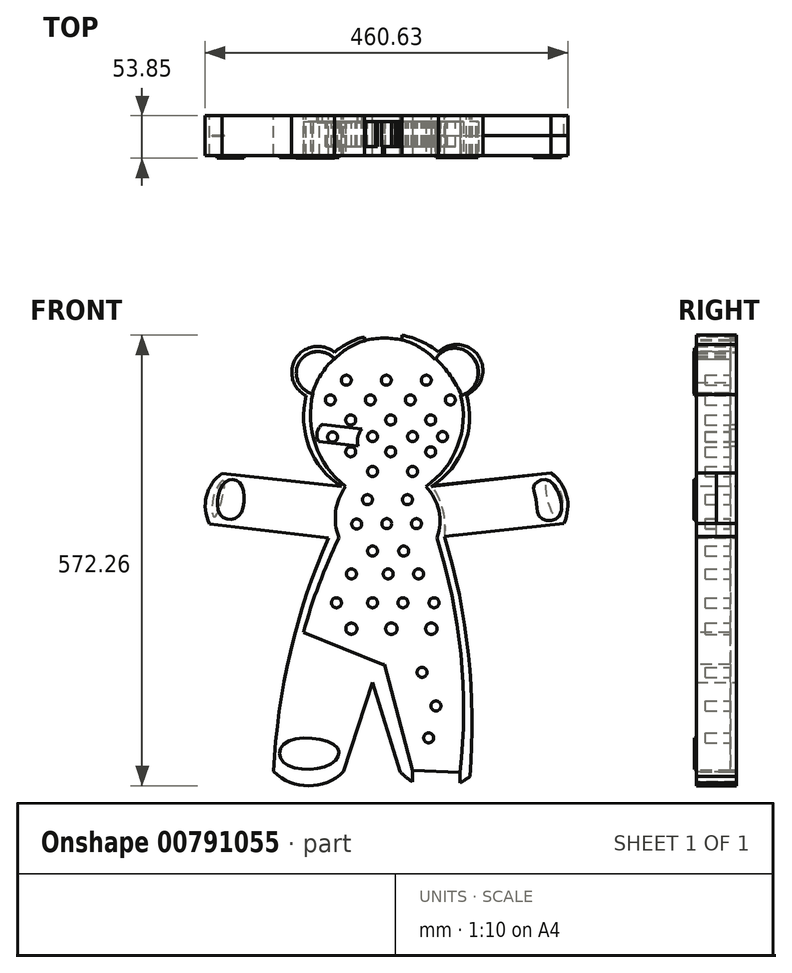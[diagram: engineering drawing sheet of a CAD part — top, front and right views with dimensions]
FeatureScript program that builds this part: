
annotation { "Feature Type Name" : "Feature", "Feature Type Description" : "" }
export const myFeature = defineFeature(function(context is Context, id is Id, definition is map)
    precondition{}
    {
        {
            var Q0;
            Q0=qCreatedBy(makeId("Front.planeOp"),FACE);
            var sketch = newSketch(context, id + "F0", { "sketchPlane" : qUnion([Q0])});
            skArc(sketch, "E0", {"start": v(-48.62, 60.53) * mm, "mid": v(-97.36, 52.98) * mm, "end": v(-84.24, 5.44) * mm});
            skArc(sketch, "E1", {"start": v(119.34, 6.7) * mm, "mid": v(134.68, 55.52) * mm, "end": v(83.78, 60.76) * mm});
            skArc(sketch, "E2", {"start": v(-84.24, 5.44) * mm, "mid": v(-80.59, -59.54) * mm, "end": v(-39.49, -110) * mm});
            skArc(sketch, "E3.trimOffspring", {"start": v(83.78, 60.76) * mm, "mid": v(17.54, 84.02) * mm, "end": v(-48.62, 60.53) * mm});
            skPoint(sketch, "E4.orphan", {"position": v(-45.78, 57.89) * mm});
            skPoint(sketch, "E5.orphan", {"position": v(81.22, 57.89) * mm});
            skLineSegment(sketch, "E6", {"start": v(-39.49, -110) * mm, "end": v(-190.95, -93.16) * mm});
            skLineSegment(sketch, "E7", {"start": v(74.93, -110) * mm, "end": v(226.37, -92.87) * mm});
            skArc(sketch, "E8", {"start": v(-190.95, -93.16) * mm, "mid": v(-211.02, -122.3) * mm, "end": v(-207.2, -157.48) * mm});
            skArc(sketch, "E9", {"start": v(242.9, -156.82) * mm, "mid": v(246.44, -121.8) * mm, "end": v(226.37, -92.87) * mm});
            skLineSegment(sketch, "E10", {"start": v(-207.2, -157.48) * mm, "end": v(-55.83, -175.25) * mm});
            skLineSegment(sketch, "E11", {"start": v(242.9, -156.82) * mm, "end": v(91.38, -173.24) * mm});
            skPoint(sketch, "E12.end.orphan", {"position": v(-138.9, -276.85) * mm});
            skArc(sketch, "E13.trimOffspring", {"start": v(74.93, -110) * mm, "mid": v(116.27, -58.92) * mm, "end": v(119.34, 6.7) * mm});
            skArc(sketch, "E14", {"start": v(-55.83, -175.25) * mm, "mid": v(-104.52, -320.36) * mm, "end": v(-125.58, -471.96) * mm});
            skArc(sketch, "E15", {"start": v(123.63, -478.04) * mm, "mid": v(121.78, -324.13) * mm, "end": v(91.38, -173.24) * mm});
            skArc(sketch, "E16", {"start": v(-125.58, -471.96) * mm, "mid": v(-81.13, -490.11) * mm, "end": v(-36.68, -471.96) * mm});
            skArc(sketch, "E17", {"start": v(34.73, -471.96) * mm, "mid": v(77.94, -493.21) * mm, "end": v(123.63, -478.04) * mm});
            skLineSegment(sketch, "E18", {"start": v(-36.68, -471.96) * mm, "end": v(0, -358.61) * mm});
            skLineSegment(sketch, "E19", {"start": v(0, -358.61) * mm, "end": v(34.73, -471.96) * mm});
            skSolve(sketch);
        }
        {
            var Q0;
            Q0=makeQuery(id+"F0.imprint","IMPRINT",FACE,{"disambiguationData":[TD([[makeQuery(id+"F0.imprint","IMPRINT",EDGE,{"derivedFrom":sQuery(id+"F0.wireOp",EDGE,"E0")}),1.0]])]});
            var sketch = newSketch(context, id + "F1", { "sketchPlane" : qUnion([Q0])});
            skArc(sketch, "E20", {"start": v(-40.72, -110.17) * mm, "mid": v(-55.88, -141.35) * mm, "end": v(-55.5, -176.02) * mm});
            skArc(sketch, "E21", {"start": v(91.74, -173.3) * mm, "mid": v(89.43, -139.67) * mm, "end": v(75.28, -109.08) * mm});
            skLineSegment(sketch, "E22", {"start": v(-190.93, -92.66) * mm, "end": v(-40.72, -110.17) * mm});
            skArc(sketch, "E23", {"start": v(-190.93, -92.66) * mm, "mid": v(-211, -122.25) * mm, "end": v(-206.68, -157.73) * mm});
            skLineSegment(sketch, "E24", {"start": v(-206.68, -157.73) * mm, "end": v(-55.5, -176.02) * mm});
            skLineSegment(sketch, "E25", {"start": v(75.28, -109.08) * mm, "end": v(226.9, -92.64) * mm});
            skArc(sketch, "E26", {"start": v(243.25, -155.89) * mm, "mid": v(246.19, -121.4) * mm, "end": v(226.9, -92.64) * mm});
            skLineSegment(sketch, "E27", {"start": v(91.74, -173.3) * mm, "end": v(243.25, -155.89) * mm});
            skSolve(sketch);
        }
        {
            var Q0;
            Q0 = qSketchRegion(id + "F1", true);
            extrude(context, id + "F2", {"entities" : qUnion([Q0]), "depth" : 25.4 * mm, "offsetDistance" : 25.4 * mm});
        }
        {
            var Q0;
            Q0=makeQuery(id+"F2.opExtrude","CAP_FACE",FACE,{"disambiguationData":[OSD([sQuery(id+"F1.wireOp",EDGE,"E20"),sQuery(id+"F1.wireOp",EDGE,"E22"),sQuery(id+"F1.wireOp",EDGE,"E23"),sQuery(id+"F1.wireOp",EDGE,"E24")])],"isStart":false});
            var sketch = newSketch(context, id + "F3", { "sketchPlane" : qUnion([Q0])});
            skPoint(sketch, "E28.1.internal.snap0", {"position": v(-211, -122.25) * mm});
            skFitSpline(sketch, "E28", {"points": [v(-188.59, -103.57) * mm, v(-201.98, -122.25) * mm, v(-200.23, -148.4) * mm, v(-188.59, -103.57) * mm]});
            skFitSpline(sketch, "E29", {"points": [v(221.34, -103.57) * mm, v(239.97, -122.2) * mm, v(233.56, -150.15) * mm, v(221.34, -103.57) * mm]});
            skSolve(sketch);
        }
        {
            var Q0;
            Q0 = qSketchRegion(id + "F3", true);
            extrude(context, id + "F4", {"entities" : qUnion([Q0]), "depth" : 0.64 * mm, "offsetDistance" : 25.4 * mm});
        }
        {
            var Q0;
            Q0 = qSketchRegion(id + "F0", true);
            extrude(context, id + "F5", {"entities" : qUnion([Q0]), "depth" : 50.8 * mm, "offsetDistance" : 25.4 * mm});
        }
        {
            var Q0;
            Q0=makeQuery(id+"F5.opExtrude","CAP_FACE",FACE,{"disambiguationData":[OSD([sQuery(id+"F0.wireOp",EDGE,"E0"),sQuery(id+"F0.wireOp",EDGE,"E1"),sQuery(id+"F0.wireOp",EDGE,"E2"),sQuery(id+"F0.wireOp",EDGE,"E3.trimOffspring"),sQuery(id+"F0.wireOp",EDGE,"E6"),sQuery(id+"F0.wireOp",EDGE,"E7"),sQuery(id+"F0.wireOp",EDGE,"E8"),sQuery(id+"F0.wireOp",EDGE,"E9"),sQuery(id+"F0.wireOp",EDGE,"E10"),sQuery(id+"F0.wireOp",EDGE,"E11"),sQuery(id+"F0.wireOp",EDGE,"E13.trimOffspring"),sQuery(id+"F0.wireOp",EDGE,"E14"),sQuery(id+"F0.wireOp",EDGE,"E15"),sQuery(id+"F0.wireOp",EDGE,"E16"),sQuery(id+"F0.wireOp",EDGE,"E17"),sQuery(id+"F0.wireOp",EDGE,"E18"),sQuery(id+"F0.wireOp",EDGE,"E19")])],"isStart":false});
            var sketch = newSketch(context, id + "F6", { "sketchPlane" : qUnion([Q0])});
            skArc(sketch, "E30", {"start": v(-48.96, 51.18) * mm, "mid": v(-92.39, 49.09) * mm, "end": v(-75.55, 9) * mm});
            skArc(sketch, "E31", {"start": v(111.95, 6.25) * mm, "mid": v(128.8, 52.71) * mm, "end": v(79.4, 51.18) * mm});
            skArc(sketch, "E32", {"start": v(79.4, 51.18) * mm, "mid": v(15.22, 78.96) * mm, "end": v(-48.96, 51.18) * mm});
            skArc(sketch, "E33", {"start": v(-75.55, 9) * mm, "mid": v(-72.56, -56.54) * mm, "end": v(-34.52, -110) * mm});
            skArc(sketch, "E34", {"start": v(-34.52, -110) * mm, "mid": v(-46.78, -141.6) * mm, "end": v(-42.77, -175.25) * mm});
            skLineSegment(sketch, "E35", {"start": v(-113.64, -459.27) * mm, "end": v(-62.8, -471.96) * mm});
            skLineSegment(sketch, "E36", {"start": v(-62.8, -471.96) * mm, "end": v(-7.88, -336.06) * mm});
            skLineSegment(sketch, "E37", {"start": v(-7.88, -336.06) * mm, "end": v(15.22, -336.06) * mm});
            skArc(sketch, "E38", {"start": v(67.64, -110) * mm, "mid": v(108.05, -58.83) * mm, "end": v(111.95, 6.25) * mm});
            skArc(sketch, "E39", {"start": v(81.53, -175.25) * mm, "mid": v(84.15, -140.59) * mm, "end": v(67.64, -110) * mm});
            skArc(sketch, "E40", {"start": v(-42.77, -175.25) * mm, "mid": v(-92.7, -313.64) * mm, "end": v(-113.64, -459.27) * mm});
            skArc(sketch, "E41", {"start": v(110.97, -473.45) * mm, "mid": v(112.16, -322.78) * mm, "end": v(81.53, -175.25) * mm});
            skPoint(sketch, "E42.end.orphan", {"position": v(110.97, -459.27) * mm});
            skPoint(sketch, "E43.end.orphan", {"position": v(59.66, -459.27) * mm});
            skLineSegment(sketch, "E44", {"start": v(15.22, -336.06) * mm, "end": v(50.93, -470.74) * mm});
            skLineSegment(sketch, "E45", {"start": v(50.93, -470.74) * mm, "end": v(110.97, -473.45) * mm});
            skSolve(sketch);
        }
        {
            var Q0;
            Q0 = qSketchRegion(id + "F6", true);
            extrude(context, id + "F7", {"entities" : qUnion([Q0]), "operationType" : NewBodyOperationType.REMOVE, "oppositeDirection" : true, "depth" : 43.18 * mm, "offsetDistance" : 25.4 * mm});
        }
        {
            var Q0;
            Q0=makeQuery(id+"F7.boolean.opBoolean","COPY",FACE,{"derivedFrom":makeQuery(id+"F7.opExtrude","CAP_FACE",FACE,{"disambiguationData":[OSD([sQuery(id+"F6.wireOp",EDGE,"E30"),sQuery(id+"F6.wireOp",EDGE,"E31"),sQuery(id+"F6.wireOp",EDGE,"E32"),sQuery(id+"F6.wireOp",EDGE,"E33"),sQuery(id+"F6.wireOp",EDGE,"E34"),sQuery(id+"F6.wireOp",EDGE,"6cMtbVWl-N6qq-ZgWd-0fdC-1SSSlQAl5eiu"),sQuery(id+"F6.wireOp",EDGE,"E35"),sQuery(id+"F6.wireOp",EDGE,"E36"),sQuery(id+"F6.wireOp",EDGE,"E37"),sQuery(id+"F6.wireOp",EDGE,"E43"),sQuery(id+"F6.wireOp",EDGE,"E42"),sQuery(id+"F6.wireOp",EDGE,"m1MFei8G-51Pd-RuaX-jXwv-OkuRzOX7tmb0"),sQuery(id+"F6.wireOp",EDGE,"bhJH275G-3Udi-Z7pS-tFxK-rDCHHQEsdnL1"),sQuery(id+"F6.wireOp",EDGE,"DvTYQwpm-AckJ-qG6A-KJKj-vuWKtyFOksdB")])],"isStart":false})});
            var sketch = newSketch(context, id + "F8", { "sketchPlane" : qUnion([Q0])});
            skCircle(sketch, "E46", {"center": v(-33.39, 25.01) * mm, "radius": 6.35 * mm});
            skCircle(sketch, "E47", {"center": v(17.41, 25.01) * mm, "radius": 6.35 * mm});
            skCircle(sketch, "E48", {"center": v(68.21, 25.01) * mm, "radius": 6.35 * mm});
            skPoint(sketch, "E49.center.orphan", {"position": v(-34.52, -25.48) * mm});
            skCircle(sketch, "E50", {"center": v(-2.87, 0) * mm, "radius": 6.35 * mm});
            skCircle(sketch, "E51", {"center": v(-53.67, 0) * mm, "radius": 6.35 * mm});
            skCircle(sketch, "E52", {"center": v(47.93, 0) * mm, "radius": 6.35 * mm});
            skCircle(sketch, "E53", {"center": v(98.73, 0) * mm, "radius": 6.35 * mm});
            skCircle(sketch, "E54", {"center": v(-27.75, -25.48) * mm, "radius": 6.35 * mm});
            skCircle(sketch, "E55", {"center": v(23.05, -25.48) * mm, "radius": 6.35 * mm});
            skCircle(sketch, "E56", {"center": v(73.85, -25.48) * mm, "radius": 6.35 * mm});
            skCircle(sketch, "E57", {"center": v(-50.8, -47.1) * mm, "radius": 6.35 * mm});
            skCircle(sketch, "E58", {"center": v(0, -46.65) * mm, "radius": 6.35 * mm});
            skCircle(sketch, "E59", {"center": v(50.8, -46.65) * mm, "radius": 6.35 * mm});
            skCircle(sketch, "E60", {"center": v(88.9, -46.65) * mm, "radius": 6.35 * mm});
            skCircle(sketch, "E61", {"center": v(-27.75, -65.94) * mm, "radius": 6.35 * mm});
            skCircle(sketch, "E62", {"center": v(23.05, -65.94) * mm, "radius": 6.35 * mm});
            skCircle(sketch, "E63", {"center": v(73.85, -65.94) * mm, "radius": 6.35 * mm});
            skCircle(sketch, "E64", {"center": v(50.8, -90.92) * mm, "radius": 6.35 * mm});
            skCircle(sketch, "E65", {"center": v(0, -90.92) * mm, "radius": 6.35 * mm});
            skCircle(sketch, "E66", {"center": v(-6.54, -126.75) * mm, "radius": 6.35 * mm});
            skCircle(sketch, "E67", {"center": v(0, -192.06) * mm, "radius": 6.35 * mm});
            skCircle(sketch, "E68", {"center": v(39.6, -192.06) * mm, "radius": 6.35 * mm});
            skCircle(sketch, "E69", {"center": v(-26.94, -221.05) * mm, "radius": 6.35 * mm});
            skCircle(sketch, "E70", {"center": v(19.87, -221.05) * mm, "radius": 6.35 * mm});
            skCircle(sketch, "E71", {"center": v(58.49, -221.05) * mm, "radius": 6.35 * mm});
            skCircle(sketch, "E72", {"center": v(44.26, -126.75) * mm, "radius": 6.35 * mm});
            skCircle(sketch, "E73", {"center": v(18.03, -157.24) * mm, "radius": 6.35 * mm});
            skCircle(sketch, "E74", {"center": v(-20.15, -157.7) * mm, "radius": 6.35 * mm});
            skCircle(sketch, "E75", {"center": v(55.74, -157.24) * mm, "radius": 6.35 * mm});
            skCircle(sketch, "E76", {"center": v(0, -257.64) * mm, "radius": 6.35 * mm});
            skCircle(sketch, "E77", {"center": v(-45.92, -257.64) * mm, "radius": 6.35 * mm});
            skCircle(sketch, "E78", {"center": v(38.6, -257.64) * mm, "radius": 6.35 * mm});
            skCircle(sketch, "E79", {"center": v(78.14, -257.64) * mm, "radius": 6.35 * mm});
            skCircle(sketch, "E80", {"center": v(-26.94, -290.63) * mm, "radius": 7.06 * mm});
            skCircle(sketch, "E81", {"center": v(23.86, -290.63) * mm, "radius": 7.25 * mm});
            skCircle(sketch, "E82", {"center": v(74.66, -290.63) * mm, "radius": 7.2 * mm});
            skCircle(sketch, "E83", {"center": v(62.86, -346.01) * mm, "radius": 6.35 * mm});
            skCircle(sketch, "E84", {"center": v(80.44, -388.8) * mm, "radius": 6.35 * mm});
            skCircle(sketch, "E85", {"center": v(71.27, -429.31) * mm, "radius": 6.35 * mm});
            skSolve(sketch);
        }
        {
            var Q0;
            Q0=makeQuery(id+"F5.opExtrude","CAP_FACE",FACE,{"disambiguationData":[OSD([sQuery(id+"F0.wireOp",EDGE,"E0"),sQuery(id+"F0.wireOp",EDGE,"E1"),sQuery(id+"F0.wireOp",EDGE,"E2"),sQuery(id+"F0.wireOp",EDGE,"E3.trimOffspring"),sQuery(id+"F0.wireOp",EDGE,"E6"),sQuery(id+"F0.wireOp",EDGE,"E7"),sQuery(id+"F0.wireOp",EDGE,"E8"),sQuery(id+"F0.wireOp",EDGE,"E9"),sQuery(id+"F0.wireOp",EDGE,"E10"),sQuery(id+"F0.wireOp",EDGE,"E11"),sQuery(id+"F0.wireOp",EDGE,"E13.trimOffspring"),sQuery(id+"F0.wireOp",EDGE,"E14"),sQuery(id+"F0.wireOp",EDGE,"E15"),sQuery(id+"F0.wireOp",EDGE,"E16"),sQuery(id+"F0.wireOp",EDGE,"E17"),sQuery(id+"F0.wireOp",EDGE,"E18"),sQuery(id+"F0.wireOp",EDGE,"E19")])],"isStart":false});
            var sketch = newSketch(context, id + "F9", { "sketchPlane" : qUnion([Q0])});
            skLineSegment(sketch, "E86", {"start": v(110.97, -486.5) * mm, "end": v(110.97, -473.45) * mm});
            skLineSegment(sketch, "E87", {"start": v(110.97, -473.45) * mm, "end": v(50.93, -470.74) * mm});
            skLineSegment(sketch, "E88", {"start": v(50.93, -470.74) * mm, "end": v(50.93, -485.09) * mm});
            skArc(sketch, "E89", {"start": v(50.93, -485.09) * mm, "mid": v(80.77, -493.5) * mm, "end": v(110.97, -486.5) * mm});
            skPoint(sketch, "E89.third.point", {"position": v(90.81, -369.52) * mm});
            skSolve(sketch);
        }
        {
            var Q0;
            Q0 = qSketchRegion(id + "F9", true);
            extrude(context, id + "F10", {"entities" : qUnion([Q0]), "operationType" : NewBodyOperationType.REMOVE, "oppositeDirection" : true, "depth" : 50.8 * mm, "offsetDistance" : 25.4 * mm});
        }
        {
            var Q0;
            Q0=makeQuery(id+"F8.imprint","IMPRINT",FACE,{"disambiguationData":[TD([[makeQuery(id+"F8.imprint","IMPRINT",EDGE,{"derivedFrom":sQuery(id+"F8.wireOp",EDGE,"E46")}),-1.0]])]});
            var sketch = newSketch(context, id + "F11", { "sketchPlane" : qUnion([Q0])});
            skArc(sketch, "E90", {"start": v(113.08, 5.85) * mm, "mid": v(99.1, 30.63) * mm, "end": v(80.32, 51.98) * mm});
            skArc(sketch, "E91", {"start": v(126.85, 54.5) * mm, "mid": v(102.9, 65.76) * mm, "end": v(80.32, 51.98) * mm});
            skArc(sketch, "E92", {"start": v(113.08, 5.85) * mm, "mid": v(133.06, 26.47) * mm, "end": v(126.85, 54.5) * mm});
            skSolve(sketch);
        }
        {
            var Q0;
            Q0 = qSketchRegion(id + "F11", true);
            extrude(context, id + "F12", {"entities" : qUnion([Q0]), "operationType" : NewBodyOperationType.ADD, "depth" : 45.72 * mm, "offsetDistance" : 25.4 * mm});
        }
        {
            var Q0;
            Q0=makeQuery(id+"F8.imprint","IMPRINT",FACE,{"disambiguationData":[TD([[makeQuery(id+"F8.imprint","IMPRINT",EDGE,{"derivedFrom":sQuery(id+"F8.wireOp",EDGE,"E46")}),-1.0]])]});
            var sketch = newSketch(context, id + "F13", { "sketchPlane" : qUnion([Q0])});
            skLineSegment(sketch, "E93", {"start": v(-90.32, -294.26) * mm, "end": v(14.72, -336.81) * mm});
            skLineSegment(sketch, "E94", {"start": v(14.72, -336.81) * mm, "end": v(-14.42, -364.03) * mm});
            skLineSegment(sketch, "E95", {"start": v(-14.42, -364.03) * mm, "end": v(-57.73, -478.26) * mm});
            skLineSegment(sketch, "E96", {"start": v(-57.73, -478.26) * mm, "end": v(-119.07, -462.55) * mm});
            skLineSegment(sketch, "E97", {"start": v(-119.07, -462.55) * mm, "end": v(-99.52, -316.11) * mm});
            skLineSegment(sketch, "E98", {"start": v(-99.52, -316.11) * mm, "end": v(-90.32, -294.26) * mm});
            skSolve(sketch);
        }
        {
            var Q0;
            Q0 = qSketchRegion(id + "F13", true);
            extrude(context, id + "F14", {"entities" : qUnion([Q0]), "operationType" : NewBodyOperationType.ADD, "depth" : 43.18 * mm, "offsetDistance" : 25.4 * mm});
        }
        {
            var Q0;
            Q0=makeQuery(id+"F8.imprint","IMPRINT",FACE,{"disambiguationData":[TD([[makeQuery(id+"F8.imprint","IMPRINT",EDGE,{"derivedFrom":sQuery(id+"F8.wireOp",EDGE,"E46")}),-1.0]])]});
            var sketch = newSketch(context, id + "F15", { "sketchPlane" : qUnion([Q0])});
            skArc(sketch, "E99", {"start": v(-48.58, 52.45) * mm, "mid": v(-65.65, 32.13) * mm, "end": v(-76.6, 7.96) * mm});
            skArc(sketch, "E100", {"start": v(-92.72, 49.08) * mm, "mid": v(-95.03, 24.45) * mm, "end": v(-76.6, 7.96) * mm});
            skArc(sketch, "E101", {"start": v(-48.58, 52.45) * mm, "mid": v(-71.46, 61.32) * mm, "end": v(-92.72, 49.08) * mm});
            skSolve(sketch);
        }
        {
            var Q0;
            Q0 = qSketchRegion(id + "F15", true);
            extrude(context, id + "F16", {"entities" : qUnion([Q0]), "operationType" : NewBodyOperationType.ADD, "depth" : 46.23 * mm, "offsetDistance" : 25.4 * mm});
        }
        {
            var Q0;
            Q0=makeQuery(id+"F14.boolean.opBoolean","MERGE",FACE,{"derivedFrom":[makeQuery(id+"F5.opExtrude","CAP_FACE",FACE,{"disambiguationData":[OSD([sQuery(id+"F0.wireOp",EDGE,"E0"),sQuery(id+"F0.wireOp",EDGE,"E1"),sQuery(id+"F0.wireOp",EDGE,"E2"),sQuery(id+"F0.wireOp",EDGE,"E3.trimOffspring"),sQuery(id+"F0.wireOp",EDGE,"E6"),sQuery(id+"F0.wireOp",EDGE,"E7"),sQuery(id+"F0.wireOp",EDGE,"E8"),sQuery(id+"F0.wireOp",EDGE,"E9"),sQuery(id+"F0.wireOp",EDGE,"E10"),sQuery(id+"F0.wireOp",EDGE,"E11"),sQuery(id+"F0.wireOp",EDGE,"E13.trimOffspring"),sQuery(id+"F0.wireOp",EDGE,"E14"),sQuery(id+"F0.wireOp",EDGE,"E15"),sQuery(id+"F0.wireOp",EDGE,"E16"),sQuery(id+"F0.wireOp",EDGE,"E17"),sQuery(id+"F0.wireOp",EDGE,"E18"),sQuery(id+"F0.wireOp",EDGE,"E19")])],"isStart":false}),makeQuery(id+"F14.opExtrude","CAP_FACE",FACE,{"disambiguationData":[OSD([sQuery(id+"F13.wireOp",EDGE,"E93"),sQuery(id+"F13.wireOp",EDGE,"E94"),sQuery(id+"F13.wireOp",EDGE,"E95"),sQuery(id+"F13.wireOp",EDGE,"E96"),sQuery(id+"F13.wireOp",EDGE,"E97"),sQuery(id+"F13.wireOp",EDGE,"E98")])],"isStart":false})]});
            var sketch = newSketch(context, id + "F17", { "sketchPlane" : qUnion([Q0])});
            skFitSpline(sketch, "E102", {"points": [v(207.4, -125.6) * mm, v(205.46, -108.48) * mm, v(224.67, -102.47) * mm, v(237.3, -147.14) * mm, v(213.35, -149.36) * mm, v(207.4, -125.6) * mm]});
            skSolve(sketch);
        }
        {
            var Q0;
            Q0 = qSketchRegion(id + "F17", true);
            extrude(context, id + "F18", {"entities" : qUnion([Q0]), "operationType" : NewBodyOperationType.ADD, "depth" : 2.3 * mm, "offsetDistance" : 25.4 * mm});
        }
        {
            var Q0;
            Q0=makeQuery(id+"F14.boolean.opBoolean","MERGE",FACE,{"derivedFrom":[makeQuery(id+"F5.opExtrude","CAP_FACE",FACE,{"disambiguationData":[OSD([sQuery(id+"F0.wireOp",EDGE,"E0"),sQuery(id+"F0.wireOp",EDGE,"E1"),sQuery(id+"F0.wireOp",EDGE,"E2"),sQuery(id+"F0.wireOp",EDGE,"E3.trimOffspring"),sQuery(id+"F0.wireOp",EDGE,"E6"),sQuery(id+"F0.wireOp",EDGE,"E7"),sQuery(id+"F0.wireOp",EDGE,"E8"),sQuery(id+"F0.wireOp",EDGE,"E9"),sQuery(id+"F0.wireOp",EDGE,"E10"),sQuery(id+"F0.wireOp",EDGE,"E11"),sQuery(id+"F0.wireOp",EDGE,"E13.trimOffspring"),sQuery(id+"F0.wireOp",EDGE,"E14"),sQuery(id+"F0.wireOp",EDGE,"E15"),sQuery(id+"F0.wireOp",EDGE,"E16"),sQuery(id+"F0.wireOp",EDGE,"E17"),sQuery(id+"F0.wireOp",EDGE,"E18"),sQuery(id+"F0.wireOp",EDGE,"E19")])],"isStart":false}),makeQuery(id+"F14.opExtrude","CAP_FACE",FACE,{"disambiguationData":[OSD([sQuery(id+"F13.wireOp",EDGE,"E93"),sQuery(id+"F13.wireOp",EDGE,"E94"),sQuery(id+"F13.wireOp",EDGE,"E95"),sQuery(id+"F13.wireOp",EDGE,"E96"),sQuery(id+"F13.wireOp",EDGE,"E97"),sQuery(id+"F13.wireOp",EDGE,"E98")])],"isStart":false})]});
            var sketch = newSketch(context, id + "F19", { "sketchPlane" : qUnion([Q0])});
            skFitSpline(sketch, "E103", {"points": [v(-193.55, -145.23) * mm, v(-188.45, -105.61) * mm, v(-168.25, -106.13) * mm, v(-169.93, -147.34) * mm, v(-193.55, -145.23) * mm]});
            skSolve(sketch);
        }
        {
            var Q0;
            Q0 = qSketchRegion(id + "F19", true);
            extrude(context, id + "F20", {"entities" : qUnion([Q0]), "operationType" : NewBodyOperationType.ADD, "depth" : 3.05 * mm, "offsetDistance" : 25.4 * mm});
        }
        {
            var Q0;
            Q0=makeQuery(id+"F14.boolean.opBoolean","MERGE",FACE,{"derivedFrom":[makeQuery(id+"F5.opExtrude","CAP_FACE",FACE,{"disambiguationData":[OSD([sQuery(id+"F0.wireOp",EDGE,"E0"),sQuery(id+"F0.wireOp",EDGE,"E1"),sQuery(id+"F0.wireOp",EDGE,"E2"),sQuery(id+"F0.wireOp",EDGE,"E3.trimOffspring"),sQuery(id+"F0.wireOp",EDGE,"E6"),sQuery(id+"F0.wireOp",EDGE,"E7"),sQuery(id+"F0.wireOp",EDGE,"E8"),sQuery(id+"F0.wireOp",EDGE,"E9"),sQuery(id+"F0.wireOp",EDGE,"E10"),sQuery(id+"F0.wireOp",EDGE,"E11"),sQuery(id+"F0.wireOp",EDGE,"E13.trimOffspring"),sQuery(id+"F0.wireOp",EDGE,"E14"),sQuery(id+"F0.wireOp",EDGE,"E15"),sQuery(id+"F0.wireOp",EDGE,"E16"),sQuery(id+"F0.wireOp",EDGE,"E17"),sQuery(id+"F0.wireOp",EDGE,"E18"),sQuery(id+"F0.wireOp",EDGE,"E19")])],"isStart":false}),makeQuery(id+"F14.opExtrude","CAP_FACE",FACE,{"disambiguationData":[OSD([sQuery(id+"F13.wireOp",EDGE,"E93"),sQuery(id+"F13.wireOp",EDGE,"E94"),sQuery(id+"F13.wireOp",EDGE,"E95"),sQuery(id+"F13.wireOp",EDGE,"E96"),sQuery(id+"F13.wireOp",EDGE,"E97"),sQuery(id+"F13.wireOp",EDGE,"E98")])],"isStart":false})]});
            var sketch = newSketch(context, id + "F21", { "sketchPlane" : qUnion([Q0])});
            skFitSpline(sketch, "E104", {"points": [v(-113.32, -460.27) * mm, v(-53.34, -462.74) * mm, v(-45.97, -440.68) * mm, v(-109.69, -435.06) * mm, v(-113.32, -460.27) * mm]});
            skSolve(sketch);
        }
        {
            var Q0;
            Q0 = qSketchRegion(id + "F21", true);
            extrude(context, id + "F22", {"entities" : qUnion([Q0]), "operationType" : NewBodyOperationType.ADD, "depth" : 2.54 * mm, "offsetDistance" : 25.4 * mm});
        }
        {
            var Q0;
            Q0=makeQuery(id+"F14.boolean.opBoolean","MERGE",FACE,{"derivedFrom":[makeQuery(id+"F5.opExtrude","CAP_FACE",FACE,{"disambiguationData":[OSD([sQuery(id+"F0.wireOp",EDGE,"E0"),sQuery(id+"F0.wireOp",EDGE,"E1"),sQuery(id+"F0.wireOp",EDGE,"E2"),sQuery(id+"F0.wireOp",EDGE,"E3.trimOffspring"),sQuery(id+"F0.wireOp",EDGE,"E6"),sQuery(id+"F0.wireOp",EDGE,"E7"),sQuery(id+"F0.wireOp",EDGE,"E8"),sQuery(id+"F0.wireOp",EDGE,"E9"),sQuery(id+"F0.wireOp",EDGE,"E10"),sQuery(id+"F0.wireOp",EDGE,"E11"),sQuery(id+"F0.wireOp",EDGE,"E13.trimOffspring"),sQuery(id+"F0.wireOp",EDGE,"E14"),sQuery(id+"F0.wireOp",EDGE,"E15"),sQuery(id+"F0.wireOp",EDGE,"E16"),sQuery(id+"F0.wireOp",EDGE,"E17"),sQuery(id+"F0.wireOp",EDGE,"E18"),sQuery(id+"F0.wireOp",EDGE,"E19")])],"isStart":false}),makeQuery(id+"F14.opExtrude","CAP_FACE",FACE,{"disambiguationData":[OSD([sQuery(id+"F13.wireOp",EDGE,"E93"),sQuery(id+"F13.wireOp",EDGE,"E94"),sQuery(id+"F13.wireOp",EDGE,"E95"),sQuery(id+"F13.wireOp",EDGE,"E96"),sQuery(id+"F13.wireOp",EDGE,"E97"),sQuery(id+"F13.wireOp",EDGE,"E98")])],"isStart":false})]});
            var sketch = newSketch(context, id + "F23", { "sketchPlane" : qUnion([Q0])});
            skPoint(sketch, "E105.first.point", {"position": v(-10.51, 80.17) * mm});
            skPoint(sketch, "E105.second.point", {"position": v(37.47, 82.15) * mm});
            skPoint(sketch, "E105.third.point", {"position": v(18, -64.5) * mm});
            skPoint(sketch, "E106.third.point", {"position": v(18, 82.15) * mm});
            skArc(sketch, "E107", {"start": v(37.47, 82.15) * mm, "mid": v(13.36, 83.93) * mm, "end": v(-10.51, 80.17) * mm});
            skPoint(sketch, "E107.third.point", {"position": v(81.32, -105.52) * mm});
            skArc(sketch, "E108", {"start": v(37.6, 76.07) * mm, "mid": v(13.48, 78.5) * mm, "end": v(-10.51, 75.12) * mm});
            skPoint(sketch, "E108.first.point", {"position": v(-10.51, 75.12) * mm});
            skPoint(sketch, "E108.second.point", {"position": v(37.6, 76.07) * mm});
            skPoint(sketch, "E108.third.point", {"position": v(82.52, -97.8) * mm});
            skLineSegment(sketch, "E109", {"start": v(-10.51, 80.17) * mm, "end": v(-10.51, 75.12) * mm});
            skLineSegment(sketch, "E110", {"start": v(37.47, 82.15) * mm, "end": v(37.6, 76.07) * mm});
            skSolve(sketch);
        }
        {
            var Q0;
            Q0 = qSketchRegion(id + "F23", true);
            extrude(context, id + "F24", {"entities" : qUnion([Q0]), "operationType" : NewBodyOperationType.REMOVE, "depth" : 50.8 * mm, "offsetDistance" : 25.4 * mm});
        }
        {
            var Q0;
            Q0 = qSketchRegion(id + "F23", true);
            extrude(context, id + "F25", {"entities" : qUnion([Q0]), "operationType" : NewBodyOperationType.REMOVE, "oppositeDirection" : true, "depth" : 50.8 * mm, "offsetDistance" : 25.4 * mm});
        }
        {
            var Q0;
            Q0 = qSketchRegion(id + "F8", true);
            extrude(context, id + "F26", {"entities" : qUnion([Q0]), "operationType" : NewBodyOperationType.ADD, "depth" : 31.75 * mm, "offsetDistance" : 25.4 * mm});
        }
        {
            var Q0;
            Q0=makeQuery(id+"F2.opExtrude","SWEPT_BODY",BODY,{"disambiguationData":[OSD([sQuery(id+"F1.wireOp",EDGE,"E20"),sQuery(id+"F1.wireOp",EDGE,"E22"),sQuery(id+"F1.wireOp",EDGE,"E23"),sQuery(id+"F1.wireOp",EDGE,"E24")])]});
            var Q1;
            Q1=qCreatedBy(makeId("Origin.pointOp"),VERTEX);
            var Q2;
            Q2=qCreatedBy(makeId("Origin.pointOp"),VERTEX);
            transform(context, id + "F27", {"entities" : qUnion([Q0]), "transformType" : TransformType.SCALE_UNIFORMLY, "scale" : .3333, "scalePoint" : qUnion([Q2]), "makeCopy" : false});
        }
    });
